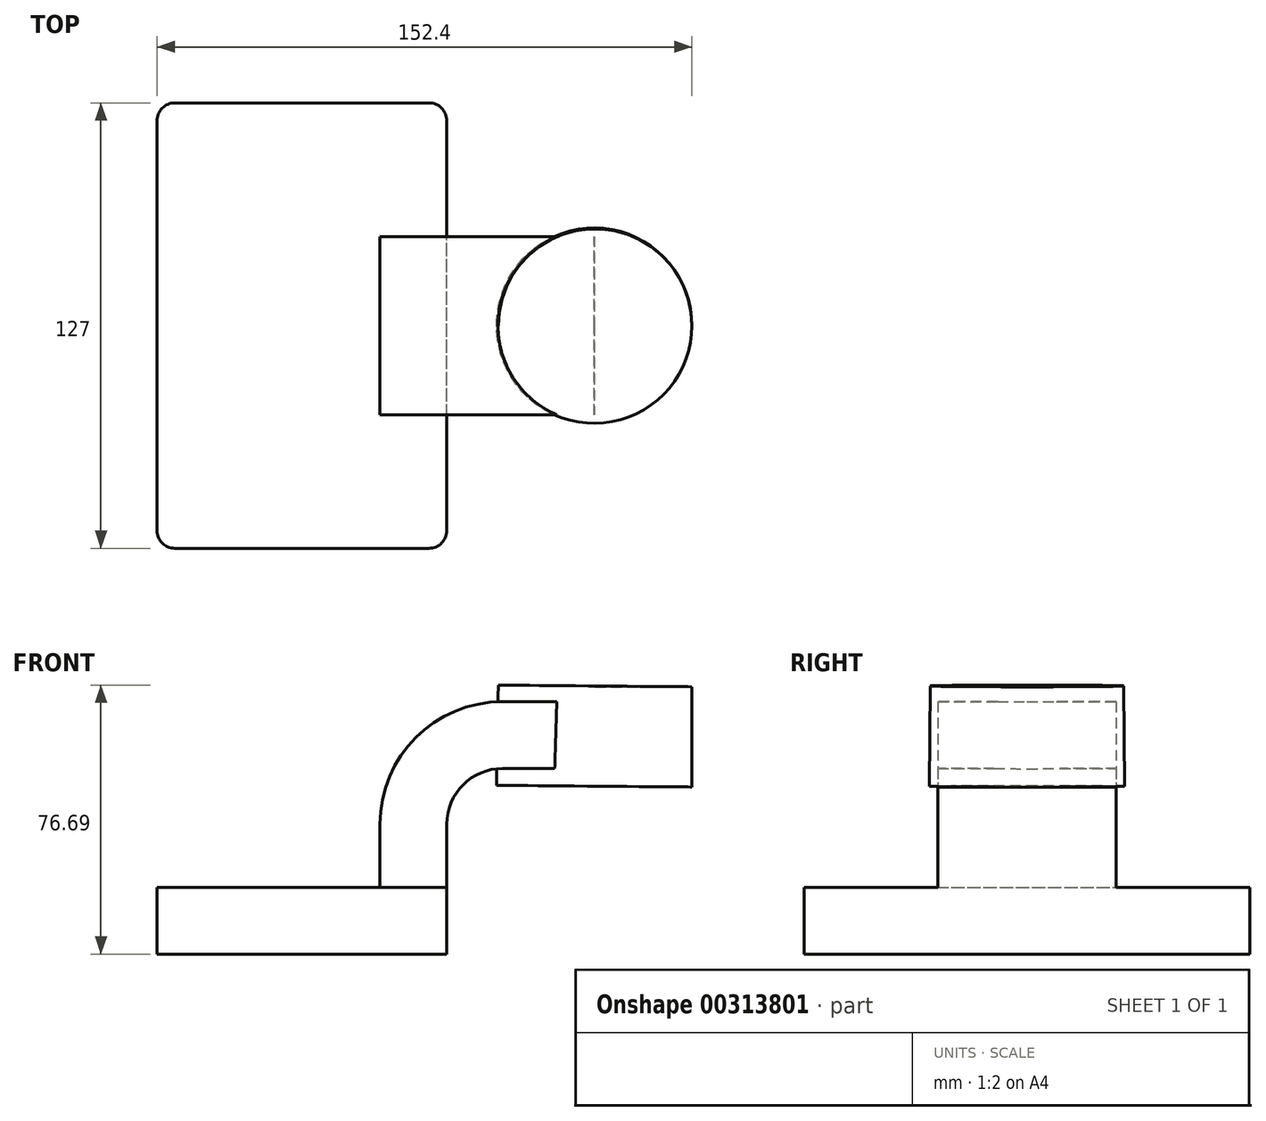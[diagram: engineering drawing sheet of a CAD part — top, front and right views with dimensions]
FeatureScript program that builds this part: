
annotation { "Feature Type Name" : "Feature", "Feature Type Description" : "" }
export const myFeature = defineFeature(function(context is Context, id is Id, definition is map)
    precondition{}
    {
        {
            var Q0;
            Q0=qCreatedBy(makeId("Front.planeOp"),FACE);
            var sketch = newSketch(context, id + "F0", { "sketchPlane" : qUnion([Q0])});
            skLineSegment(sketch, "E0.bottom", {"start": v(41.27, 9.53) * mm, "end": v(-41.28, 9.53) * mm});
            skLineSegment(sketch, "E0.top", {"start": v(41.28, -9.52) * mm, "end": v(-41.27, -9.52) * mm});
            skLineSegment(sketch, "E0.left", {"start": v(41.27, 9.53) * mm, "end": v(41.28, -9.52) * mm});
            skLineSegment(sketch, "E0.right", {"start": v(-41.28, 9.53) * mm, "end": v(-41.27, -9.52) * mm});
            skPoint(sketch, "E0.middle", {"position": v(0, 0) * mm});
            skLineSegment(sketch, "E1.bottom", {"start": v(111.12, 38.1) * mm, "end": v(60.33, 38.1) * mm});
            skLineSegment(sketch, "E1.top", {"start": v(111.12, 66.68) * mm, "end": v(60.33, 66.68) * mm});
            skLineSegment(sketch, "E1.left", {"start": v(111.12, 38.1) * mm, "end": v(111.12, 66.68) * mm});
            skLineSegment(sketch, "E1.right", {"start": v(60.33, 38.1) * mm, "end": v(60.33, 66.68) * mm});
            skPoint(sketch, "E1.middle", {"position": v(85.72, 52.39) * mm});
            skLineSegment(sketch, "E2", {"start": v(41.27, 9.53) * mm, "end": v(41.27, 27.5) * mm});
            skArc(sketch, "E3", {"start": v(41.27, 27.5) * mm, "mid": v(45.92, 38.73) * mm, "end": v(57.15, 43.38) * mm});
            skLineSegment(sketch, "E4", {"start": v(57.15, 43.38) * mm, "end": v(83.28, 43.38) * mm});
            skLineSegment(sketch, "E5.0", {"start": v(57.15, 62.43) * mm, "end": v(83.53, 62.43) * mm});
            skArc(sketch, "E5.1", {"start": v(22.22, 27.5) * mm, "mid": v(32.45, 52.2) * mm, "end": v(57.15, 62.43) * mm});
            skLineSegment(sketch, "E5.2", {"start": v(22.22, 9.53) * mm, "end": v(22.22, 27.5) * mm});
            skFitSpline(sketch, "E6", {"points": [v(-41.28, 9.53) * mm, v(57.15, 62.43) * mm], "startDerivative": vector(40.26, 82.28) * mm, "endDerivative": vector(188.37, -17.05) * mm});
            skLineSegment(sketch, "E7", {"start": v(83.28, 43.38) * mm, "end": v(83.28, 38.1) * mm});
            skLineSegment(sketch, "E8", {"start": v(83.28, 38.1) * mm, "end": v(83.53, 66.68) * mm});
            skSolve(sketch);
        }
        {
            var Q0;
            Q0=makeQuery(id+"F0.imprint","IMPRINT",FACE,{"disambiguationData":[TD([[makeQuery(id+"F0.imprint","IMPRINT",EDGE,{"derivedFrom":sQuery(id+"F0.wireOp",EDGE,"E0.top")}),-1.0]])]});
            extrude(context, id + "F1", {"entities" : qUnion([Q0]), "depth" : 127 * mm, "symmetric" : true});
        }
        {
            var Q0;
            {var subQ1=sQuery(id+"F0.wireOp",EDGE,"E2");Q0=makeQuery(id+"F0.imprint","IMPRINT",FACE,{"disambiguationData":[TD([[makeQuery(id+"F0.imprint","IMPRINT",EDGE,{"derivedFrom":subQ1}),1.0]])]});}
            var Q1;
            {var subQ0=sQuery(id+"F0.wireOp",EDGE,"E4");var subQ1=sQuery(id+"F0.wireOp",EDGE,"E1.right");var subQ2=makeQuery(id+"F0.imprint","INTERSECT",VERTEX,{"derivedFrom":[subQ1,subQ0]});Q1=makeQuery(id+"F0.imprint","IMPRINT",FACE,{"disambiguationData":[TD([[makeQuery(id+"F0.imprint","IMPRINT",EDGE,{"disambiguationData":[TD([[subQ2,-1.0]])],"derivedFrom":subQ1}),-1.0]])]});}
            extrude(context, id + "F2", {"entities" : qUnion([Q0, Q1]), "operationType" : NewBodyOperationType.ADD, "depth" : 50.8 * mm, "symmetric" : true});
        }
        {
            var Q0;
            Q0=makeQuery(id+"F0.imprint","IMPRINT",FACE,{"disambiguationData":[TD([[makeQuery(id+"F0.imprint","IMPRINT",EDGE,{"derivedFrom":sQuery(id+"F0.wireOp",EDGE,"E5.1")}),1.0]])]});
            extrude(context, id + "F3", {"entities" : qUnion([Q0]), "operationType" : NewBodyOperationType.ADD, "depth" : 15.88 * mm, "symmetric" : true});
        }
        {
            var Q0;
            {var subQ4=sQuery(id+"F0.wireOp",EDGE,"E1.left");Q0=makeQuery(id+"F0.imprint","IMPRINT",FACE,{"disambiguationData":[TD([[makeQuery(id+"F0.imprint","IMPRINT",EDGE,{"derivedFrom":subQ4}),1.0]])]});}
            var Q1;
            Q1=sQuery(id+"F0.wireOp",EDGE,"E8");
            revolve(context, id + "F4", {"operationType" : NewBodyOperationType.ADD, "entities" : qUnion([Q0]), "axis" : qUnion([Q1]), "revolveType" : RevolveType.FULL});
        }
        {
            var Q0;
            Q0=makeQuery(id+"F1.opExtrude","CAP_EDGE",EDGE,{"disambiguationData":[OSD([sQuery(id+"F0.wireOp",EDGE,"E0.left")])],"isStart":false});
            var Q1;
            Q1=makeQuery(id+"F1.opExtrude","CAP_EDGE",EDGE,{"disambiguationData":[OSD([sQuery(id+"F0.wireOp",EDGE,"E0.right")])],"isStart":false});
            var Q2;
            Q2=makeQuery(id+"F1.opExtrude","CAP_EDGE",EDGE,{"disambiguationData":[OSD([sQuery(id+"F0.wireOp",EDGE,"E0.left")])],"isStart":true});
            var Q3;
            Q3=makeQuery(id+"F1.opExtrude","CAP_EDGE",EDGE,{"disambiguationData":[OSD([sQuery(id+"F0.wireOp",EDGE,"E0.right")])],"isStart":true});
            fillet(context, id + "F5", {"entities" : qUnion([Q0, Q1, Q2, Q3]), "radius" : 5.08 * mm, "tangentPropagation" : true, "allowEdgeOverflow" : false});
        }
    });
